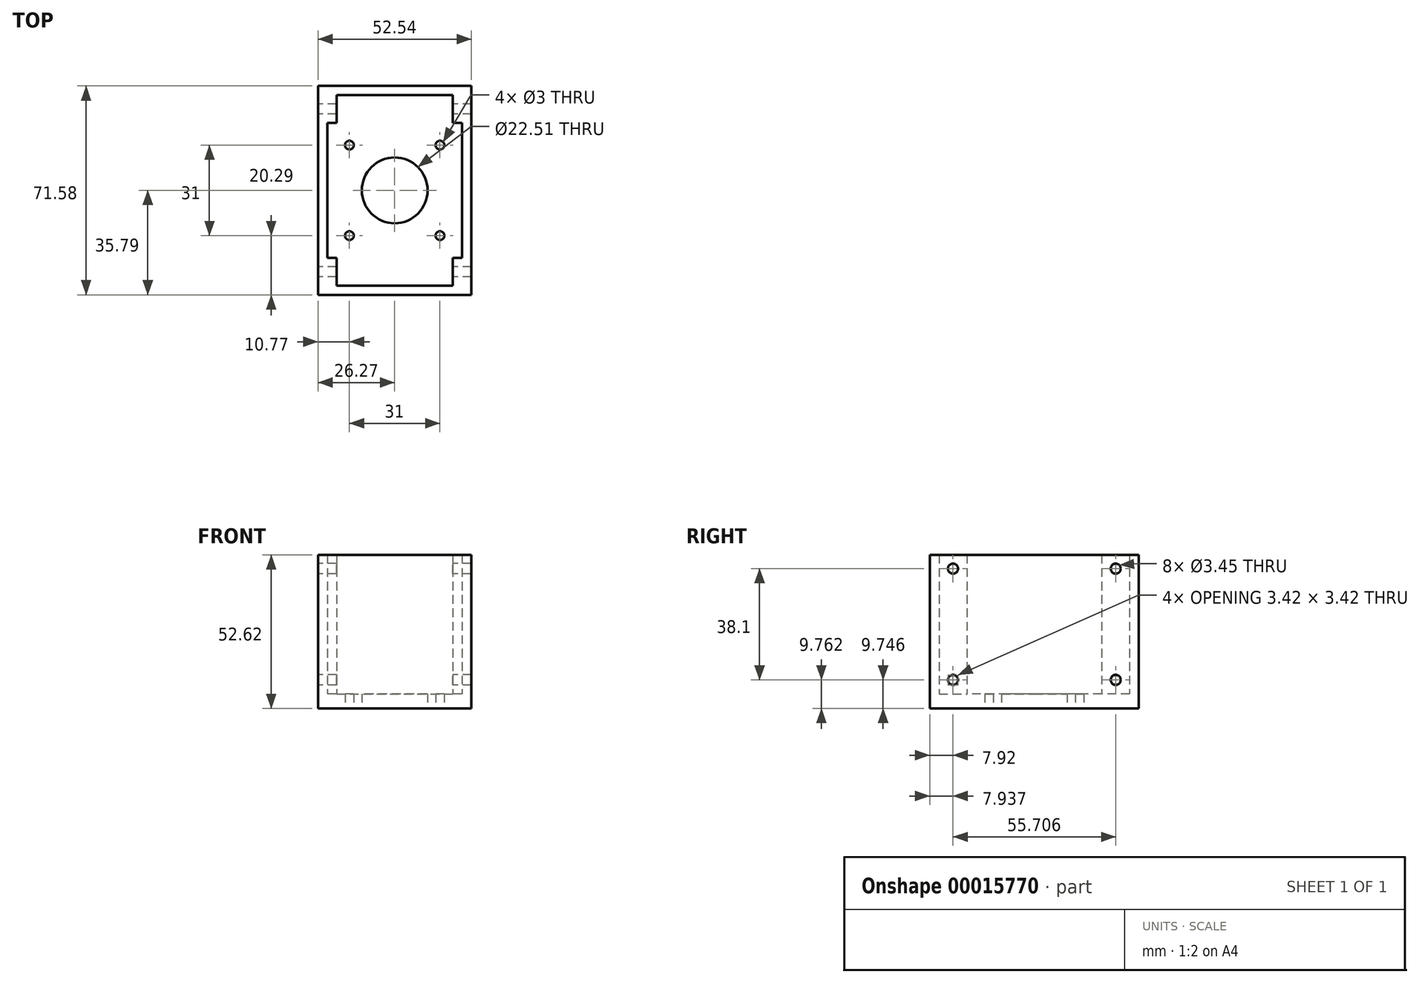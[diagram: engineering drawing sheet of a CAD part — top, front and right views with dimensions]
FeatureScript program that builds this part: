
annotation { "Feature Type Name" : "Feature", "Feature Type Description" : "" }
export const myFeature = defineFeature(function(context is Context, id is Id, definition is map)
    precondition{}
    {
        {
            var Q0;
            Q0=qCreatedBy(makeId("Top.planeOp"),FACE);
            var sketch = newSketch(context, id + "F0", { "sketchPlane" : qUnion([Q0])});
            skLineSegment(sketch, "E0.bottom", {"start": v(26.27, -35.8) * mm, "end": v(-26.27, -35.8) * mm});
            skLineSegment(sketch, "E0.top", {"start": v(26.27, 35.8) * mm, "end": v(-26.27, 35.8) * mm});
            skLineSegment(sketch, "E0.left", {"start": v(26.27, -35.8) * mm, "end": v(26.27, 35.8) * mm});
            skLineSegment(sketch, "E0.right", {"start": v(-26.27, -35.8) * mm, "end": v(-26.27, 35.8) * mm});
            skPoint(sketch, "E0.middle", {"position": v(0, 0) * mm});
            skLineSegment(sketch, "E1.bottom", {"start": v(-15.5, 15.5) * mm, "end": v(15.5, 15.5) * mm, "construction": true});
            skLineSegment(sketch, "E1.top", {"start": v(-15.5, -15.5) * mm, "end": v(15.5, -15.5) * mm, "construction": true});
            skLineSegment(sketch, "E1.left", {"start": v(-15.5, 15.5) * mm, "end": v(-15.5, -15.5) * mm, "construction": true});
            skLineSegment(sketch, "E1.right", {"start": v(15.5, 15.5) * mm, "end": v(15.5, -15.5) * mm, "construction": true});
            skCircle(sketch, "E2", {"center": v(0, 0) * mm, "radius": 11.25 * mm});
            skCircle(sketch, "E3", {"center": v(15.5, -15.5) * mm, "radius": 1.5 * mm});
            skCircle(sketch, "E4", {"center": v(15.5, 15.5) * mm, "radius": 1.5 * mm});
            skCircle(sketch, "E5", {"center": v(-15.5, 15.5) * mm, "radius": 1.5 * mm});
            skCircle(sketch, "E6", {"center": v(-15.5, -15.5) * mm, "radius": 1.5 * mm});
            skSolve(sketch);
        }
        {
            var Q0;
            Q0 = qSketchRegion(id + "F0", true);
            extrude(context, id + "F1", {"entities" : qUnion([Q0]), "depth" : 5 * mm});
        }
        {
            var Q0;
            Q0=makeQuery(id+"F1.opExtrude","CAP_FACE",FACE,{"disambiguationData":[OSD([sQuery(id+"F0.wireOp",EDGE,"E0.bottom"),sQuery(id+"F0.wireOp",EDGE,"E0.top"),sQuery(id+"F0.wireOp",EDGE,"E0.left"),sQuery(id+"F0.wireOp",EDGE,"E0.right"),sQuery(id+"F0.wireOp",EDGE,"E2"),sQuery(id+"F0.wireOp",EDGE,"E3"),sQuery(id+"F0.wireOp",EDGE,"E4"),sQuery(id+"F0.wireOp",EDGE,"E5"),sQuery(id+"F0.wireOp",EDGE,"E6")])],"isStart":false});
            var sketch = newSketch(context, id + "F2", { "sketchPlane" : qUnion([Q0])});
            skLineSegment(sketch, "E7.bottom", {"start": v(-26.27, 35.8) * mm, "end": v(26.27, 35.8) * mm});
            skLineSegment(sketch, "E7.top", {"start": v(-26.27, -35.8) * mm, "end": v(26.27, -35.8) * mm});
            skLineSegment(sketch, "E7.left", {"start": v(-26.27, 35.8) * mm, "end": v(-26.27, -35.8) * mm});
            skLineSegment(sketch, "E7.right", {"start": v(26.27, 35.8) * mm, "end": v(26.27, -35.8) * mm});
            skPoint(sketch, "E8.middle", {"position": v(0, 0) * mm});
            skLineSegment(sketch, "E9", {"start": v(-19.92, 32.62) * mm, "end": v(-19.92, 35.8) * mm, "construction": true});
            skLineSegment(sketch, "E10", {"start": v(-19.92, 32.62) * mm, "end": v(-26.27, 32.62) * mm, "construction": true});
            skLineSegment(sketch, "E11", {"start": v(-19.92, 32.62) * mm, "end": v(19.92, 32.62) * mm});
            skLineSegment(sketch, "E12", {"start": v(-19.92, 32.62) * mm, "end": v(-19.92, 23.1) * mm});
            skLineSegment(sketch, "E13", {"start": v(-19.92, 23.1) * mm, "end": v(-23.1, 23.1) * mm});
            skLineSegment(sketch, "E14", {"start": v(-23.1, 23.1) * mm, "end": v(-23.1, -23.1) * mm});
            skLineSegment(sketch, "E15", {"start": v(19.92, 32.62) * mm, "end": v(19.92, 23.1) * mm});
            skLineSegment(sketch, "E16", {"start": v(19.92, 23.1) * mm, "end": v(23.1, 23.1) * mm});
            skLineSegment(sketch, "E17", {"start": v(23.1, 23.1) * mm, "end": v(23.1, -23.1) * mm});
            skLineSegment(sketch, "E18", {"start": v(23.1, -23.1) * mm, "end": v(19.92, -23.1) * mm});
            skLineSegment(sketch, "E19", {"start": v(19.92, -23.1) * mm, "end": v(19.92, -32.62) * mm});
            skLineSegment(sketch, "E20", {"start": v(19.92, -32.62) * mm, "end": v(-19.92, -32.62) * mm});
            skLineSegment(sketch, "E21", {"start": v(19.92, -32.62) * mm, "end": v(26.27, -32.62) * mm, "construction": true});
            skLineSegment(sketch, "E22", {"start": v(19.92, -32.62) * mm, "end": v(19.92, -35.8) * mm, "construction": true});
            skLineSegment(sketch, "E23", {"start": v(-19.92, -32.62) * mm, "end": v(-19.92, -23.1) * mm});
            skLineSegment(sketch, "E24", {"start": v(-19.92, -23.1) * mm, "end": v(-23.1, -23.1) * mm});
            skSolve(sketch);
        }
        {
            var Q0;
            Q0 = qSketchRegion(id + "F2", true);
            extrude(context, id + "F3", {"entities" : qUnion([Q0]), "operationType" : NewBodyOperationType.ADD, "depth" : 47.62 * mm});
        }
        {
            var Q0;
            Q0=makeQuery(id+"F3.boolean.opBoolean","MERGE",FACE,{"derivedFrom":[makeQuery(id+"F1.opExtrude","SWEPT_FACE",FACE,{"disambiguationData":[OSD([sQuery(id+"F0.wireOp",EDGE,"E0.right")])]}),makeQuery(id+"F3.opExtrude","SWEPT_FACE",FACE,{"disambiguationData":[OSD([sQuery(id+"F2.wireOp",EDGE,"E7.left")])]})]});
            var sketch = newSketch(context, id + "F4", { "sketchPlane" : qUnion([Q0])});
            skLineSegment(sketch, "E25.bottom", {"start": v(-27.85, 47.86) * mm, "end": v(27.85, 47.86) * mm, "construction": true});
            skLineSegment(sketch, "E25.top", {"start": v(-27.85, 9.76) * mm, "end": v(27.85, 9.76) * mm, "construction": true});
            skLineSegment(sketch, "E25.left", {"start": v(-27.85, 47.86) * mm, "end": v(-27.85, 9.76) * mm, "construction": true});
            skLineSegment(sketch, "E25.right", {"start": v(27.85, 47.86) * mm, "end": v(27.85, 9.76) * mm, "construction": true});
            skCircle(sketch, "E26", {"center": v(-27.85, 47.86) * mm, "radius": 1.73 * mm});
            skCircle(sketch, "E27", {"center": v(27.85, 47.86) * mm, "radius": 1.73 * mm});
            skCircle(sketch, "E28", {"center": v(27.85, 9.76) * mm, "radius": 1.73 * mm});
            skCircle(sketch, "E29", {"center": v(-27.85, 9.76) * mm, "radius": 1.73 * mm});
            skLineSegment(sketch, "E30", {"start": v(27.85, 47.86) * mm, "end": v(27.85, 52.63) * mm, "construction": true});
            skLineSegment(sketch, "E31", {"start": v(-27.85, 47.86) * mm, "end": v(-27.85, 52.63) * mm, "construction": true});
            skLineSegment(sketch, "E32", {"start": v(0, 9.76) * mm, "end": v(0, 5) * mm, "construction": true});
            skSolve(sketch);
        }
        {
            var Q0;
            Q0 = qSketchRegion(id + "F4", true);
            var Q1;
            Q1=makeQuery(id+"F3.boolean.opBoolean","MERGE",FACE,{"derivedFrom":[makeQuery(id+"F1.opExtrude","SWEPT_FACE",FACE,{"disambiguationData":[OSD([sQuery(id+"F0.wireOp",EDGE,"E0.left")])]}),makeQuery(id+"F3.opExtrude","SWEPT_FACE",FACE,{"disambiguationData":[OSD([sQuery(id+"F2.wireOp",EDGE,"E7.right")])]})]});
            extrude(context, id + "F5", {"entities" : qUnion([Q0]), "operationType" : NewBodyOperationType.REMOVE, "endBound" : BoundingType.UP_TO_SURFACE, "oppositeDirection" : true, "endBoundEntityFace" : qUnion([Q1]), "depth" : 25.4 * mm});
        }
    });
